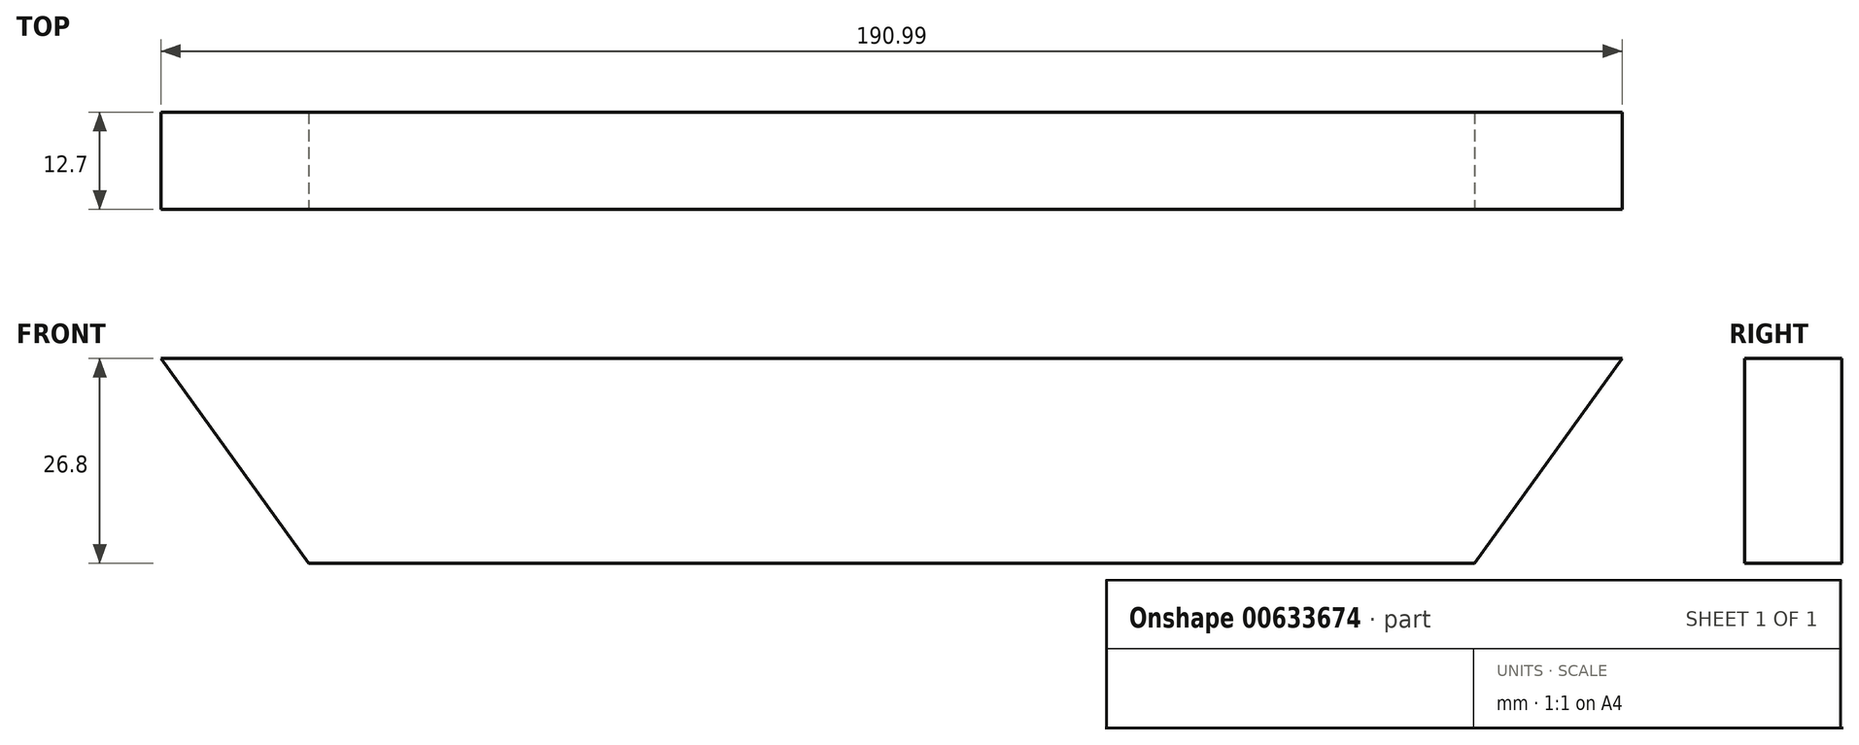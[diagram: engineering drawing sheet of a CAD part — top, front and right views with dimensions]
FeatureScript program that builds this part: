
annotation { "Feature Type Name" : "Feature", "Feature Type Description" : "" }
export const myFeature = defineFeature(function(context is Context, id is Id, definition is map)
    precondition{}
    {
        {
            var Q0;
            Q0=qCreatedBy(makeId("Front.planeOp"),FACE);
            var sketch = newSketch(context, id + "F0", { "sketchPlane" : qUnion([Q0])});
            skLineSegment(sketch, "E0", {"start": v(-87.51, -26.8) * mm, "end": v(64.89, -26.8) * mm});
            skLineSegment(sketch, "E1", {"start": v(64.89, -26.8) * mm, "end": v(84.18, 0) * mm});
            skLineSegment(sketch, "E2.MirrorCS", {"start": v(-87.51, -26.8) * mm, "end": v(-106.8, 0) * mm});
            skLineSegment(sketch, "E3", {"start": v(-106.8, 0) * mm, "end": v(84.18, 0) * mm});
            skSolve(sketch);
        }
        {
            var Q0;
            Q0=makeQuery(id+"F0.imprint","IMPRINT",FACE,{"disambiguationData":[TD([[makeQuery(id+"F0.imprint","IMPRINT",EDGE,{"derivedFrom":sQuery(id+"F0.wireOp",EDGE,"E0")}),1.0]])]});
            extrude(context, id + "F1", {"entities" : qUnion([Q0]), "oppositeDirection" : true, "depth" : 12.7 * mm, "offsetDistance" : 25.4 * mm});
        }
    });
